# Revit family: KHL_Kemlux-Celing
name_source: partatom
category: Lighting Fixtures
revit_build: Autodesk Revit 2013 (Build: 20130531_2115(x64)
units: mm (PartAtom-declared; Revit-internal decimal feet)

## types (9) — shared parameters
Color Filter = 16777215
Default Elevation = 4' - 0"
Description = Class I, Division 2 LED Fixture Series
Dimming Lamp Color Temperature Shift = <None>
Emit Shape Visible in Rendering = No
Emit from Circle Diameter = 0' - 11"
Load Classification = Lighting
Manufacturer = Hubbell Industrial Lighting
Model = KHL - Kemlux III LED
Photometric Web Link = http://www.hubbellindustrial.com
Power Factor = 1
Product Documentation Link = http://cdn.hubbellindustrial.com
Product Page URL = http://www.hubbellindustrial.com
Tilt Angle = -90.00°
URL = http://www.hubbellindustrial.com
Voltage = 277 V

## per-type parameters (varying)
| type | Apparent Load | Glass | Lamp | Material Finish | Optics | Photometric Web File | Watt | Wattage Comments |
| KHL-18L-X-5K-5M | 43 VA | Hubbell - White Glass | 18 High Performanc LEDs | Hubbell - Tan | Type V Square | KXL-18L-X-5K-5M.ies | 43 W | 43 Watts, 18 LEDs |
| KHL-18L-X-5K-5R | 43 VA | <By Category> | 18 High Performanc LEDs | <By Category> | Type V Rectangle | KXL-18L-X-5K-5R.ies | 43 W | 43 Watts, 18 LEDs |
| KHL-18L-X-5K-N | 43 VA | <By Category> | 18 High Performanc LEDs | <By Category> | Narrow | KXL-18L-X-5K-N.ies | 43 W | 43 Watts, 18 LEDs |
| KHL-24L-X-5K-5M | 57 VA | <By Category> | 24 High Performanc LEDs | <By Category> | Type V Square | KXL-24L-X-5K-5M.ies | 57 W | 57 Watts, 24 LEDs |
| KHL-24L-X-5K-5R | 57 VA | <By Category> | 24 High Performanc LEDs | <By Category> | Type V Rectangle | KXL-24L-X-5K-5R.ies | 57 W | 57 Watts, 24 LEDs |
| KHL-24L-X-5K-N | 57 VA | <By Category> | 24 High Performanc LEDs | <By Category> | Narrow | KXL-24L-X-5K-N.ies | 57 W | 57 Watts, 24 LEDs |
| KHL-36L-X-5K-5M | 86 VA | <By Category> | 36 High Performanc LEDs | <By Category> | Type V Square | KXL-36L-X-5K-5M.ies | 86 W | 86 Watts, 36 LEDs |
| KHL-36L-X-5K-5R | 86 VA | <By Category> | 36 High Performanc LEDs | <By Category> | Type V Rectangle | KXL-36L-X-5K-5R.ies | 86 W | 86 Watts, 36 LEDs |
| KHL-36L-X-5K-N | 86 VA | <By Category> | 36 High Performanc LEDs | <By Category> | Type V Rectangle | KXL-36L-X-5K-N.ies | 86 W | 86 Watts, 36 LEDs |

## geometry (parser evidence)
native form markers: Sweep x6
no freeform markers — native parametric forms only
